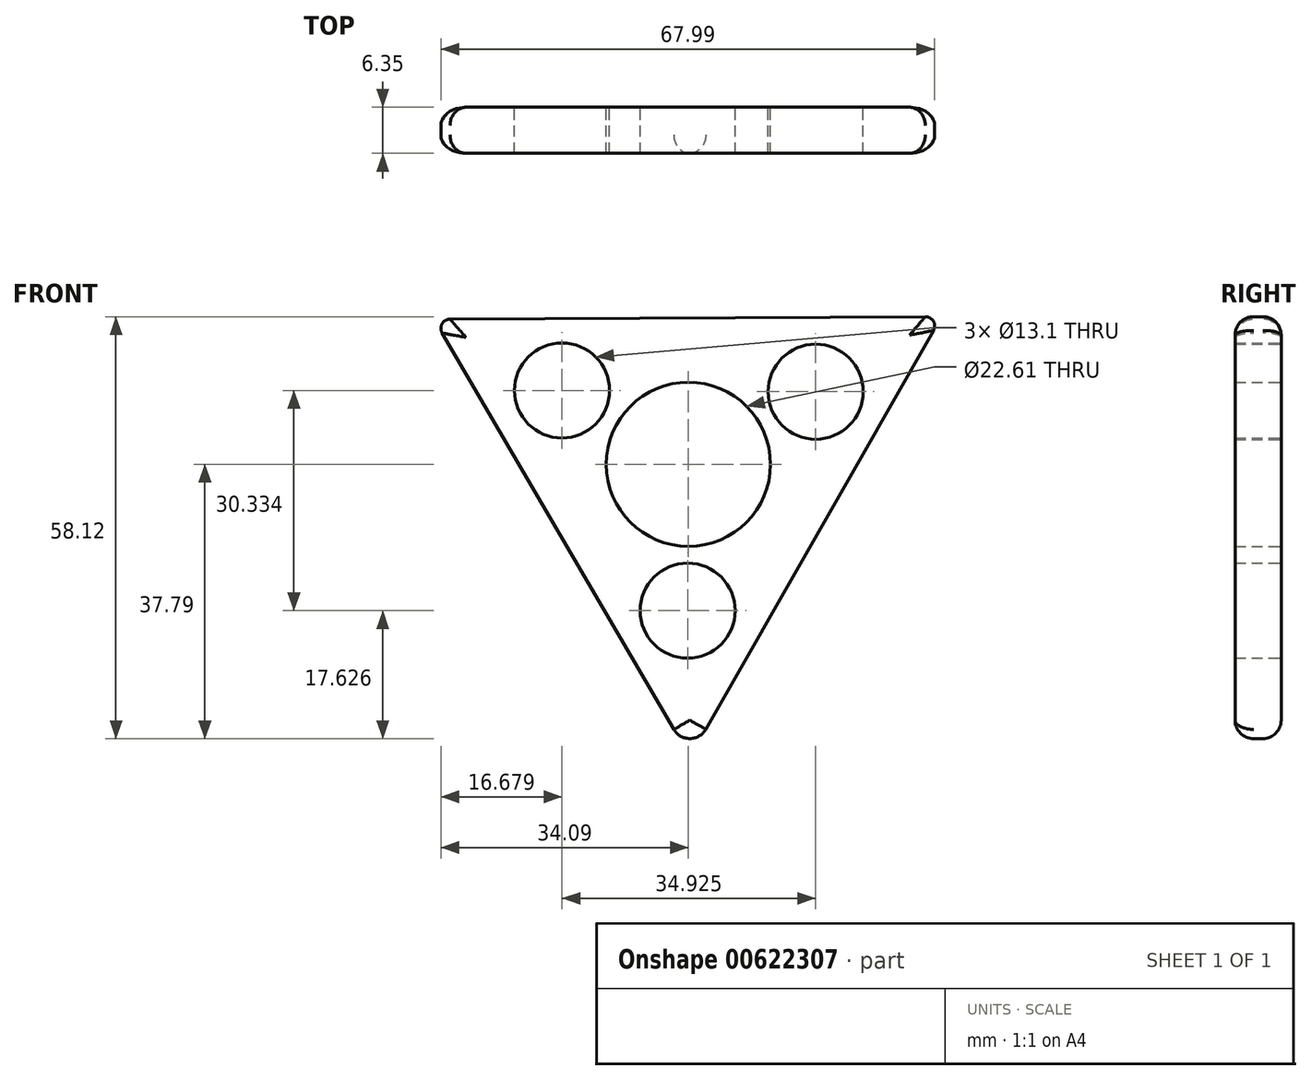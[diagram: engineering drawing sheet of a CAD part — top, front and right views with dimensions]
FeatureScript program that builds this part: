
annotation { "Feature Type Name" : "Feature", "Feature Type Description" : "" }
export const myFeature = defineFeature(function(context is Context, id is Id, definition is map)
    precondition{}
    {
        {
            var Q0;
            Q0=qCreatedBy(makeId("Front.planeOp"),FACE);
            var sketch = newSketch(context, id + "F0", { "sketchPlane" : qUnion([Q0])});
            skCircle(sketch, "E0", {"center": v(0, 0) * mm, "radius": 11.3 * mm});
            skCircle(sketch, "E1.cCircle", {"center": v(0, 0) * mm, "radius": 20.16 * mm, "construction": true});
            skLineSegment(sketch, "E1.0", {"start": v(34.82, 20.34) * mm, "end": v(0.2, -40.33) * mm});
            skLineSegment(sketch, "E1.1", {"start": v(0.2, -40.33) * mm, "end": v(-35.03, 19.99) * mm});
            skLineSegment(sketch, "E1.2", {"start": v(-35.03, 19.99) * mm, "end": v(34.82, 20.34) * mm});
            skPoint(sketch, "E1.0.midPoint", {"position": v(17.51, -10) * mm});
            skCircle(sketch, "E2", {"center": v(17.51, 10) * mm, "radius": 6.55 * mm});
            skCircle(sketch, "E3.1.0", {"center": v(-17.41, 10.17) * mm, "radius": 6.55 * mm});
            skCircle(sketch, "E3.2.0", {"center": v(-0.1, -20.16) * mm, "radius": 6.55 * mm});
            skSolve(sketch);
        }
        {
            var Q0;
            Q0 = qSketchRegion(id + "F0", true);
            extrude(context, id + "F1", {"entities" : qUnion([Q0]), "depth" : 6.35 * mm, "offsetDistance" : 25.4 * mm});
        }
        {
            var Q0;
            Q0=makeQuery(id+"F1.opExtrude","CAP_EDGE",EDGE,{"disambiguationData":[OSD([sQuery(id+"F0.wireOp",EDGE,"E1.0")])],"isStart":false});
            var Q1;
            Q1=makeQuery(id+"F1.opExtrude","CAP_EDGE",EDGE,{"disambiguationData":[OSD([sQuery(id+"F0.wireOp",EDGE,"E1.2")])],"isStart":false});
            var Q2;
            Q2=makeQuery(id+"F1.opExtrude","CAP_EDGE",EDGE,{"disambiguationData":[OSD([sQuery(id+"F0.wireOp",EDGE,"E1.1")])],"isStart":false});
            fillet(context, id + "F2", {"entities" : qUnion([Q0, Q1, Q2]), "radius" : 2.54 * mm, "tangentPropagation" : true, "allowEdgeOverflow" : false});
        }
        {
            var Q0;
            Q0=makeQuery(id+"F1.opExtrude","CAP_EDGE",EDGE,{"disambiguationData":[OSD([sQuery(id+"F0.wireOp",EDGE,"E1.1")])],"isStart":true});
            var Q1;
            Q1=makeQuery(id+"F1.opExtrude","CAP_EDGE",EDGE,{"disambiguationData":[OSD([sQuery(id+"F0.wireOp",EDGE,"E1.2")])],"isStart":true});
            var Q2;
            Q2=makeQuery(id+"F1.opExtrude","CAP_EDGE",EDGE,{"disambiguationData":[OSD([sQuery(id+"F0.wireOp",EDGE,"E1.0")])],"isStart":true});
            var Q3;
            {var subQ0=sQuery(id+"F0.wireOp",EDGE,"E1.1");Q3=makeQuery(id+"F2.opFillet","BLEND_EDGE",EDGE,{"blendedFrom":[makeQuery(id+"F1.opExtrude","CAP_EDGE",EDGE,{"disambiguationData":[OSD([subQ0])],"isStart":false}),makeQuery(id+"F1.opExtrude","SWEPT_FACE",FACE,{"disambiguationData":[OSD([subQ0])]})],"blendedInto":[makeQuery(id+"F1.opExtrude","SWEPT_FACE",FACE,{"disambiguationData":[OSD([subQ0])]})]});}
            var Q4;
            Q4=makeQuery(id+"F1.opExtrude","SWEPT_EDGE",EDGE,{"disambiguationData":[OSD([sQuery(id+"F0.wireOp",EDGE,"E1.0"),sQuery(id+"F0.wireOp",EDGE,"E1.1")])]});
            fillet(context, id + "F3", {"entities" : qUnion([Q0, Q1, Q2, Q3, Q4]), "radius" : 2.54 * mm, "tangentPropagation" : true, "allowEdgeOverflow" : false});
        }
        {
            var Q0;
            Q0=makeQuery(id+"F1.opExtrude","SWEPT_EDGE",EDGE,{"disambiguationData":[OSD([sQuery(id+"F0.wireOp",EDGE,"E1.0"),sQuery(id+"F0.wireOp",EDGE,"E1.2")])]});
            var Q1;
            Q1=makeQuery(id+"F1.opExtrude","SWEPT_EDGE",EDGE,{"disambiguationData":[OSD([sQuery(id+"F0.wireOp",EDGE,"E1.1"),sQuery(id+"F0.wireOp",EDGE,"E1.2")])]});
            fillet(context, id + "F4", {"entities" : qUnion([Q0, Q1]), "radius" : 1.27 * mm, "tangentPropagation" : true, "allowEdgeOverflow" : false});
        }
    });
